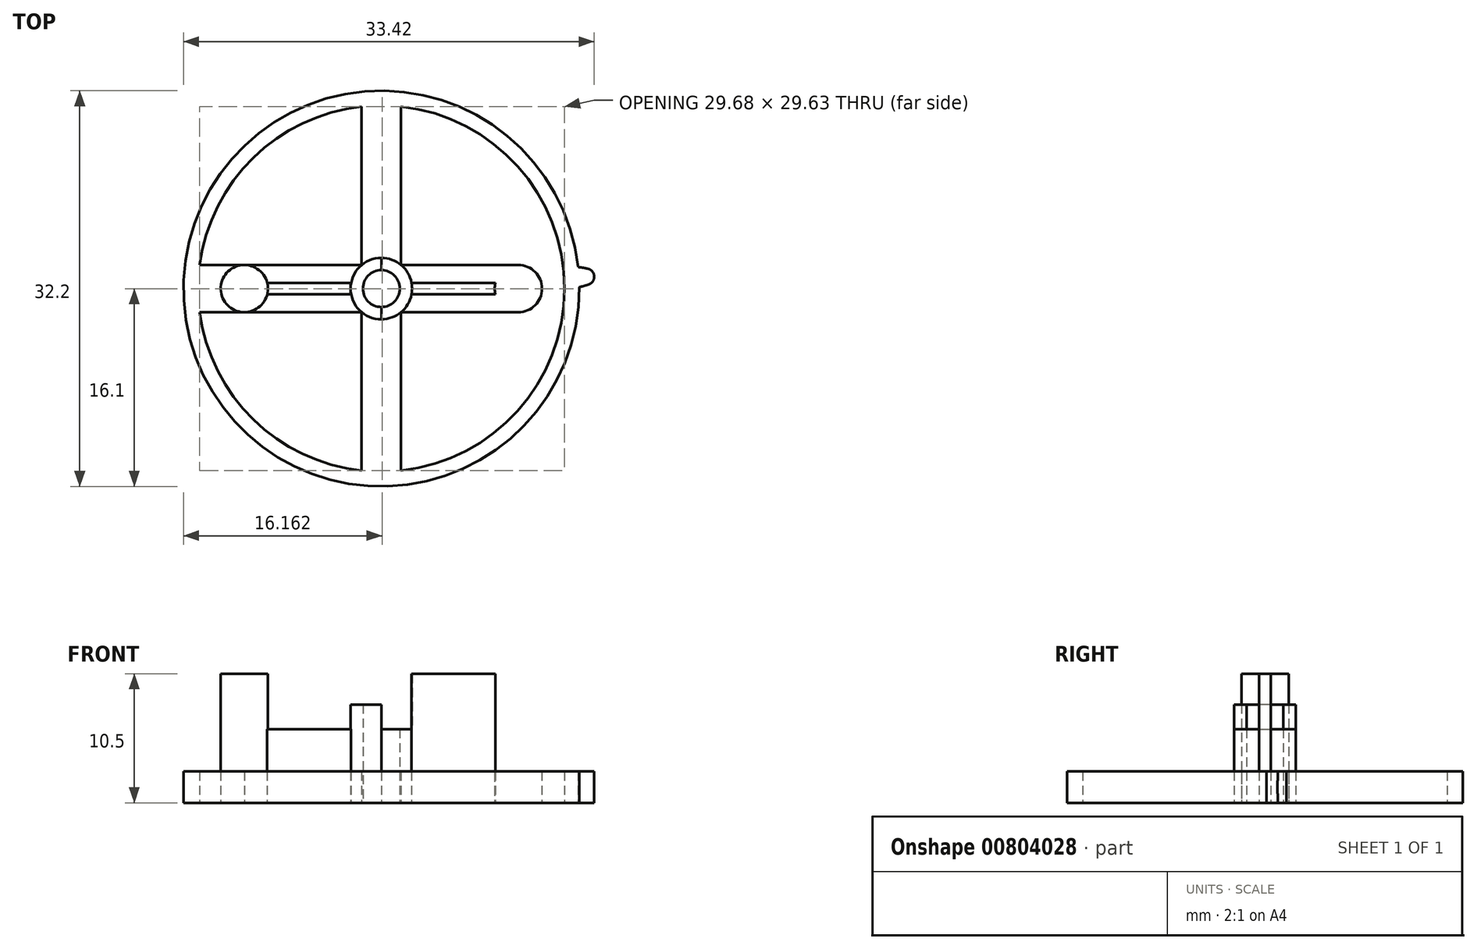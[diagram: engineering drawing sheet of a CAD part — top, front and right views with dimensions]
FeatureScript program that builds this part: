
annotation { "Feature Type Name" : "Feature", "Feature Type Description" : "" }
export const myFeature = defineFeature(function(context is Context, id is Id, definition is map)
    precondition{}
    {
        {
            var Q0;
            Q0=qCreatedBy(makeId("Top.planeOp"),FACE);
            var sketch = newSketch(context, id + "F0", { "sketchPlane" : qUnion([Q0])});
            skCircle(sketch, "E0", {"center": v(-11.15, 0) * mm, "radius": 1.92 * mm});
            skCircle(sketch, "E1.MirrorC", {"center": v(11.15, 0) * mm, "radius": 1.92 * mm});
            skCircle(sketch, "E2", {"center": v(0, 0) * mm, "radius": 14.9 * mm});
            skLineSegment(sketch, "E3.bottom", {"start": v(-14.78, 1.92) * mm, "end": v(-1.6, 1.92) * mm});
            skLineSegment(sketch, "E3.top", {"start": v(-14.78, -1.92) * mm, "end": v(-1.6, -1.92) * mm});
            skCircle(sketch, "E4", {"center": v(0, 0) * mm, "radius": 2.5 * mm});
            skLineSegment(sketch, "E5", {"start": v(0, 2.5) * mm, "end": v(0, -2.5) * mm});
            skLineSegment(sketch, "E6", {"start": v(-1.6, 1.92) * mm, "end": v(-1.6, 14.81) * mm});
            skLineSegment(sketch, "E7", {"start": v(-1.6, -1.92) * mm, "end": v(-1.6, -14.81) * mm});
            skLineSegment(sketch, "E8.MirrorCS", {"start": v(1.6, 1.92) * mm, "end": v(1.6, 14.81) * mm});
            skLineSegment(sketch, "E9.MirrorCS", {"start": v(1.6, -1.92) * mm, "end": v(1.6, -14.81) * mm});
            skCircle(sketch, "E10", {"center": v(0, 0) * mm, "radius": 1.5 * mm});
            skLineSegment(sketch, "E11", {"start": v(1.6, -1.92) * mm, "end": v(14.78, -1.92) * mm});
            skLineSegment(sketch, "E12", {"start": v(1.58, 1.92) * mm, "end": v(14.78, 1.92) * mm});
            skArc(sketch, "E13.6.0", {"start": v(17.29, 1.47) * mm, "mid": v(16.65, 1.65) * mm, "end": v(16, 1.75) * mm});
            skArc(sketch, "E14.trimOffspring", {"start": v(15.76, 3.3) * mm, "mid": v(15.76, 3.3) * mm, "end": v(15.75, 3.3) * mm});
            skArc(sketch, "E15.trimOffspring", {"start": v(16.1, 0.12) * mm, "mid": v(16.73, 0.3) * mm, "end": v(17.34, 0.54) * mm});
            skArc(sketch, "E16.trimOffspring", {"start": v(17.34, 0.54) * mm, "mid": v(17.32, 1) * mm, "end": v(17.29, 1.47) * mm});
            skLineSegment(sketch, "E17", {"start": v(-9.28, 0.47) * mm, "end": v(-2.46, 0.47) * mm});
            skLineSegment(sketch, "E18.MirrorCS", {"start": v(-9.28, -0.47) * mm, "end": v(-2.46, -0.47) * mm});
            skLineSegment(sketch, "E19.MirrorCS", {"start": v(9.28, -0.47) * mm, "end": v(2.46, -0.47) * mm});
            skLineSegment(sketch, "E20.MirrorCS", {"start": v(9.28, 0.47) * mm, "end": v(2.46, 0.47) * mm});
            skArc(sketch, "E21", {"start": v(16.1, 0.12) * mm, "mid": v(16.07, 0.94) * mm, "end": v(16, 1.75) * mm});
            skArc(sketch, "E22", {"start": v(16, 1.75) * mm, "mid": v(-16.07, -0.94) * mm, "end": v(16.1, 0.12) * mm});
            skSolve(sketch);
        }
        {
            var Q0;
            {var subQ0=sQuery(id+"F0.wireOp",EDGE,"E0");var subQ2=makeQuery(id+"F0.imprint","INTERSECT",VERTEX,{"derivedFrom":[subQ0,sQuery(id+"F0.wireOp",EDGE,"E17")]});Q0=makeQuery(id+"F0.imprint","IMPRINT",FACE,{"disambiguationData":[TD([[makeQuery(id+"F0.imprint","IMPRINT",EDGE,{"disambiguationData":[TD([[subQ2,-1.0]])],"derivedFrom":subQ0}),1.0]])]});}
            var Q1;
            {var subQ0=sQuery(id+"F0.wireOp",EDGE,"E1.MirrorC");var subQ2=makeQuery(id+"F0.imprint","INTERSECT",VERTEX,{"derivedFrom":[subQ0,sQuery(id+"F0.wireOp",EDGE,"E20.MirrorCS")]});Q1=makeQuery(id+"F0.imprint","IMPRINT",FACE,{"disambiguationData":[TD([[makeQuery(id+"F0.imprint","IMPRINT",EDGE,{"disambiguationData":[TD([[subQ2,-1.0]])],"derivedFrom":subQ0}),-1.0]])]});}
            extrude(context, id + "F1", {"entities" : qUnion([Q0, Q1]), "depth" : 10.5 * mm, "offsetDistance" : 25 * mm});
        }
        {
            var Q0;
            {var subQ1=sQuery(id+"F0.wireOp",EDGE,"E3.bottom");var subQ3=sQuery(id+"F0.wireOp",EDGE,"E5");var subQ4=makeQuery(id+"F0.imprint","INTERSECT",VERTEX,{"derivedFrom":[subQ1,subQ3]});Q0=makeQuery(id+"F0.imprint","IMPRINT",FACE,{"disambiguationData":[TD([[makeQuery(id+"F0.imprint","IMPRINT",EDGE,{"disambiguationData":[TD([[subQ4,-1.0]])],"derivedFrom":subQ3}),1.0]])]});}
            var Q1;
            {var subQ0=sQuery(id+"F0.wireOp",EDGE,"E4");var subQ3=sQuery(id+"F0.wireOp",EDGE,"E5");var subQ5=makeQuery(id+"F0.imprint","INTERSECT",VERTEX,{"disambiguationData":[OD(1.0)],"derivedFrom":[subQ0,subQ3]});Q1=makeQuery(id+"F0.imprint","IMPRINT",FACE,{"disambiguationData":[TD([[makeQuery(id+"F0.imprint","IMPRINT",EDGE,{"disambiguationData":[TD([[subQ5,1.0]])],"derivedFrom":subQ3}),1.0]])]});}
            var Q2;
            {var subQ0=sQuery(id+"F0.wireOp",EDGE,"E4");var subQ3=sQuery(id+"F0.wireOp",EDGE,"E5");var subQ5=makeQuery(id+"F0.imprint","INTERSECT",VERTEX,{"disambiguationData":[OD(0.0)],"derivedFrom":[subQ0,subQ3]});Q2=makeQuery(id+"F0.imprint","IMPRINT",FACE,{"disambiguationData":[TD([[makeQuery(id+"F0.imprint","IMPRINT",EDGE,{"disambiguationData":[TD([[subQ5,-1.0]])],"derivedFrom":subQ3}),1.0]])]});}
            var Q3;
            {var subQ0=sQuery(id+"F0.wireOp",EDGE,"E19.MirrorCS");Q3=makeQuery(id+"F0.imprint","IMPRINT",FACE,{"disambiguationData":[TD([[makeQuery(id+"F0.imprint","IMPRINT",EDGE,{"derivedFrom":subQ0}),-1.0]])]});}
            var Q4;
            {var subQ0=sQuery(id+"F0.wireOp",EDGE,"E18.MirrorCS");Q4=makeQuery(id+"F0.imprint","IMPRINT",FACE,{"disambiguationData":[TD([[makeQuery(id+"F0.imprint","IMPRINT",EDGE,{"derivedFrom":subQ0}),1.0]])]});}
            extrude(context, id + "F2", {"entities" : qUnion([Q0, Q1, Q2, Q3, Q4]), "operationType" : NewBodyOperationType.ADD, "depth" : 6 * mm, "offsetDistance" : 25 * mm});
        }
        {
            var Q0;
            {var subQ0=sQuery(id+"F0.wireOp",EDGE,"E5");var subQ1=sQuery(id+"F0.wireOp",EDGE,"E3.bottom");var subQ2=makeQuery(id+"F0.imprint","INTERSECT",VERTEX,{"derivedFrom":[subQ1,subQ0]});Q0=makeQuery(id+"F0.imprint","IMPRINT",FACE,{"disambiguationData":[TD([[makeQuery(id+"F0.imprint","IMPRINT",EDGE,{"disambiguationData":[TD([[subQ2,-1.0]])],"derivedFrom":subQ0}),-1.0]])]});}
            var Q1;
            {var subQ0=sQuery(id+"F0.wireOp",EDGE,"E4");var subQ3=sQuery(id+"F0.wireOp",EDGE,"E5");var subQ5=makeQuery(id+"F0.imprint","INTERSECT",VERTEX,{"disambiguationData":[OD(1.0)],"derivedFrom":[subQ0,subQ3]});Q1=makeQuery(id+"F0.imprint","IMPRINT",FACE,{"disambiguationData":[TD([[makeQuery(id+"F0.imprint","IMPRINT",EDGE,{"disambiguationData":[TD([[subQ5,1.0]])],"derivedFrom":subQ3}),-1.0]])]});}
            var Q2;
            {var subQ0=sQuery(id+"F0.wireOp",EDGE,"E4");var subQ3=sQuery(id+"F0.wireOp",EDGE,"E5");var subQ5=makeQuery(id+"F0.imprint","INTERSECT",VERTEX,{"disambiguationData":[OD(0.0)],"derivedFrom":[subQ0,subQ3]});Q2=makeQuery(id+"F0.imprint","IMPRINT",FACE,{"disambiguationData":[TD([[makeQuery(id+"F0.imprint","IMPRINT",EDGE,{"disambiguationData":[TD([[subQ5,-1.0]])],"derivedFrom":subQ3}),-1.0]])]});}
            extrude(context, id + "F3", {"entities" : qUnion([Q0, Q1, Q2]), "depth" : 8 * mm, "offsetDistance" : 25 * mm});
        }
        {
            var Q0;
            {var subQ8=sQuery(id+"F0.wireOp",EDGE,"bwW6kXku-kHrk-eiLk-WIoQ-2fsx9gSQarSF");var subQ11=makeQuery(id+"F0.imprint","IMPRINT",VERTEX,{"derivedFrom":subQ8});Q0=makeQuery(id+"F0.imprint","IMPRINT",FACE,{"disambiguationData":[TD([[makeQuery(id+"F0.imprint","IMPRINT",EDGE,{"disambiguationData":[TD([[subQ11,1.0]])],"derivedFrom":subQ8}),1.0]])]});}
            var Q1;
            {var subQ0=sQuery(id+"F0.wireOp",EDGE,"E3.bottom");var subQ1=sQuery(id+"F0.wireOp",EDGE,"E0");var subQ2=makeQuery(id+"F0.imprint","INTERSECT",VERTEX,{"disambiguationData":[OD(1.0)],"derivedFrom":[subQ1,subQ0]});Q1=makeQuery(id+"F0.imprint","IMPRINT",FACE,{"disambiguationData":[TD([[makeQuery(id+"F0.imprint","IMPRINT",EDGE,{"disambiguationData":[TD([[subQ2,-1.0]])],"derivedFrom":subQ1}),-1.0]])]});}
            var Q2;
            {var subQ0=sQuery(id+"F0.wireOp",EDGE,"E17");Q2=makeQuery(id+"F0.imprint","IMPRINT",FACE,{"disambiguationData":[TD([[makeQuery(id+"F0.imprint","IMPRINT",EDGE,{"derivedFrom":subQ0}),1.0]])]});}
            var Q3;
            {var subQ0=sQuery(id+"F0.wireOp",EDGE,"E18.MirrorCS");Q3=makeQuery(id+"F0.imprint","IMPRINT",FACE,{"disambiguationData":[TD([[makeQuery(id+"F0.imprint","IMPRINT",EDGE,{"derivedFrom":subQ0}),-1.0]])]});}
            var Q4;
            {var subQ0=sQuery(id+"F0.wireOp",EDGE,"E20.MirrorCS");Q4=makeQuery(id+"F0.imprint","IMPRINT",FACE,{"disambiguationData":[TD([[makeQuery(id+"F0.imprint","IMPRINT",EDGE,{"derivedFrom":subQ0}),-1.0]])]});}
            var Q5;
            {var subQ0=sQuery(id+"F0.wireOp",EDGE,"E12");var subQ1=sQuery(id+"F0.wireOp",EDGE,"E1.MirrorC");var subQ2=makeQuery(id+"F0.imprint","INTERSECT",VERTEX,{"disambiguationData":[OD(1.0)],"derivedFrom":[subQ1,subQ0]});Q5=makeQuery(id+"F0.imprint","IMPRINT",FACE,{"disambiguationData":[TD([[makeQuery(id+"F0.imprint","IMPRINT",EDGE,{"disambiguationData":[TD([[subQ2,-1.0]])],"derivedFrom":subQ1}),1.0]])]});}
            var Q6;
            {var subQ0=sQuery(id+"F0.wireOp",EDGE,"E7");Q6=makeQuery(id+"F0.imprint","IMPRINT",FACE,{"disambiguationData":[TD([[makeQuery(id+"F0.imprint","IMPRINT",EDGE,{"derivedFrom":subQ0}),1.0]])]});}
            var Q7;
            {var subQ0=sQuery(id+"F0.wireOp",EDGE,"E8.MirrorCS");Q7=makeQuery(id+"F0.imprint","IMPRINT",FACE,{"disambiguationData":[TD([[makeQuery(id+"F0.imprint","IMPRINT",EDGE,{"derivedFrom":subQ0}),1.0]])]});}
            var Q8;
            {var subQ0=sQuery(id+"F0.wireOp",EDGE,"E19.MirrorCS");Q8=makeQuery(id+"F0.imprint","IMPRINT",FACE,{"disambiguationData":[TD([[makeQuery(id+"F0.imprint","IMPRINT",EDGE,{"derivedFrom":subQ0}),1.0]])]});}
            var Q9;
            {var subQ0=sQuery(id+"F0.wireOp",EDGE,"E13.6.0");Q9=makeQuery(id+"F0.imprint","IMPRINT",FACE,{"disambiguationData":[TD([[makeQuery(id+"F0.imprint","IMPRINT",EDGE,{"derivedFrom":subQ0}),1.0]])]});}
            var Q10;
            {var subQ6=sQuery(id+"F0.wireOp",EDGE,"E21");Q10=makeQuery(id+"F0.imprint","IMPRINT",FACE,{"disambiguationData":[TD([[makeQuery(id+"F0.imprint","IMPRINT",EDGE,{"derivedFrom":subQ6}),1.0]])]});}
            extrude(context, id + "F4", {"entities" : qUnion([Q0, Q1, Q2, Q3, Q4, Q5, Q6, Q7, Q8, Q9, Q10]), "depth" : 2.55 * mm, "offsetDistance" : 25 * mm});
        }
        {
            var Q0;
            Q0=makeQuery(id+"F4.opExtrude","SWEPT_EDGE",EDGE,{"disambiguationData":[OSD([sQuery(id+"F0.wireOp",EDGE,"E15.trimOffspring"),sQuery(id+"F0.wireOp",EDGE,"E16.trimOffspring")])]});
            var Q1;
            Q1=makeQuery(id+"F4.opExtrude","SWEPT_EDGE",EDGE,{"disambiguationData":[OSD([sQuery(id+"F0.wireOp",EDGE,"E13.6.0"),sQuery(id+"F0.wireOp",EDGE,"E16.trimOffspring")])]});
            fillet(context, id + "F5", {"entities" : qUnion([Q0, Q1]), "radius" : 0.72 * mm, "tangentPropagation" : true, "rho" : 0.5, "crossSection" : FilletCrossSection.CONIC, "allowEdgeOverflow" : false});
        }
    });
